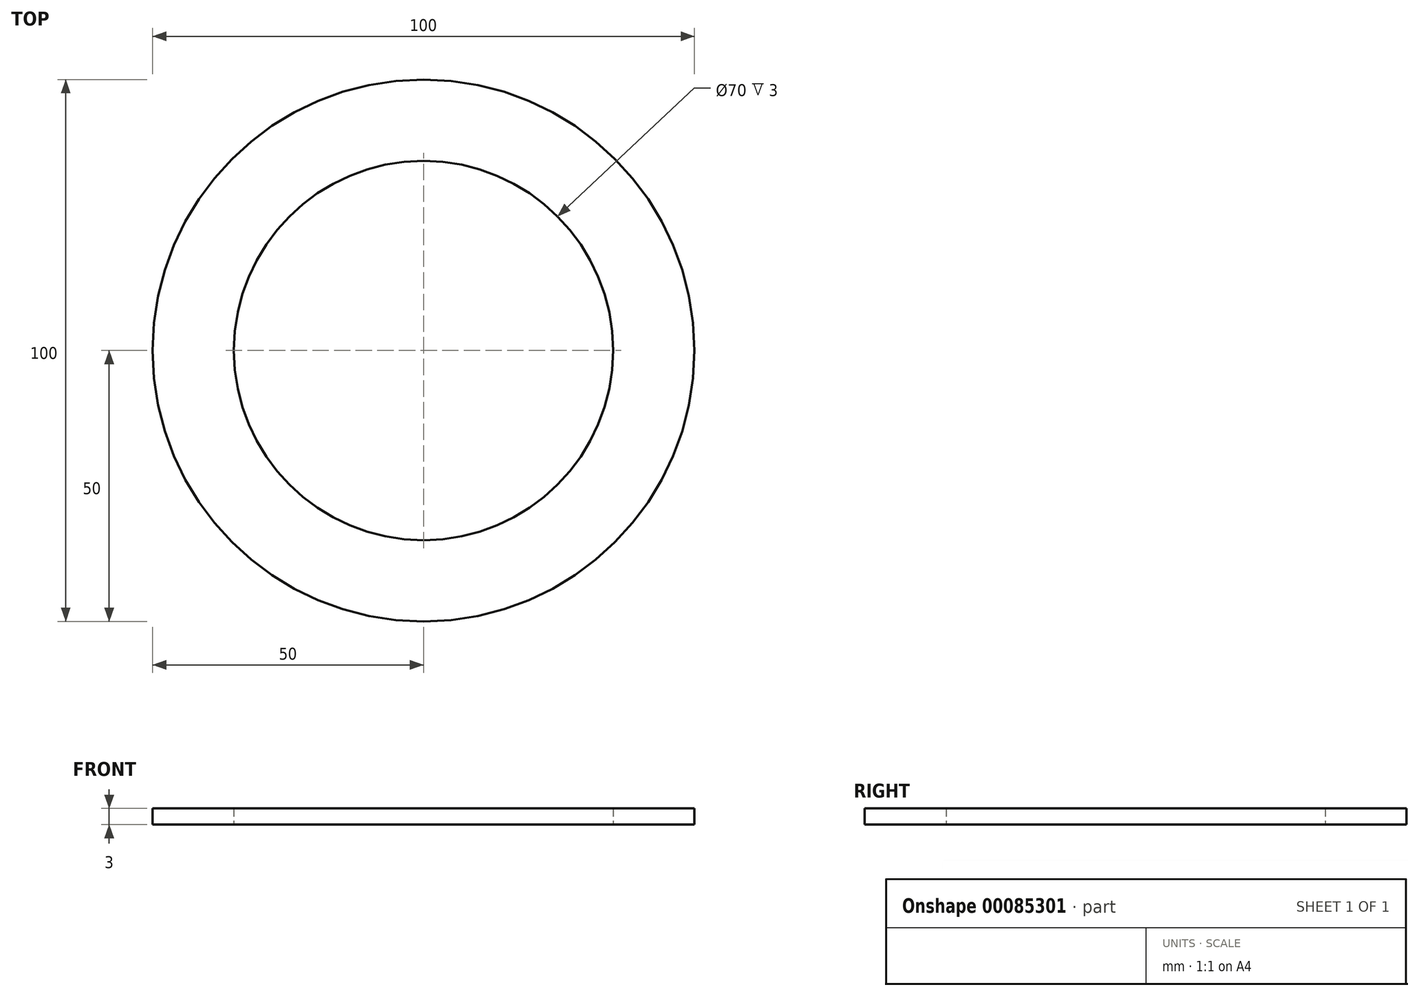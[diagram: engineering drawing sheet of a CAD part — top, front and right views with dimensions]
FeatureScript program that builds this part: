
annotation { "Feature Type Name" : "Feature", "Feature Type Description" : "" }
export const myFeature = defineFeature(function(context is Context, id is Id, definition is map)
    precondition{}
    {
        {
            var Q0;
            Q0=qCreatedBy(makeId("Top.planeOp"),FACE);
            var sketch = newSketch(context, id + "F0", { "sketchPlane" : qUnion([Q0])});
            skCircle(sketch, "E0", {"center": v(0, 0) * mm, "radius": 50 * mm});
            skCircle(sketch, "E1.0", {"center": v(0, 0) * mm, "radius": 35 * mm});
            skSolve(sketch);
        }
        {
            var Q0;
            Q0=qSketchRegion(id+"F0",true);
            extrude(context, id + "F1", {"entities" : qUnion([Q0]), "depth" : 3 * mm});
        }
    });
